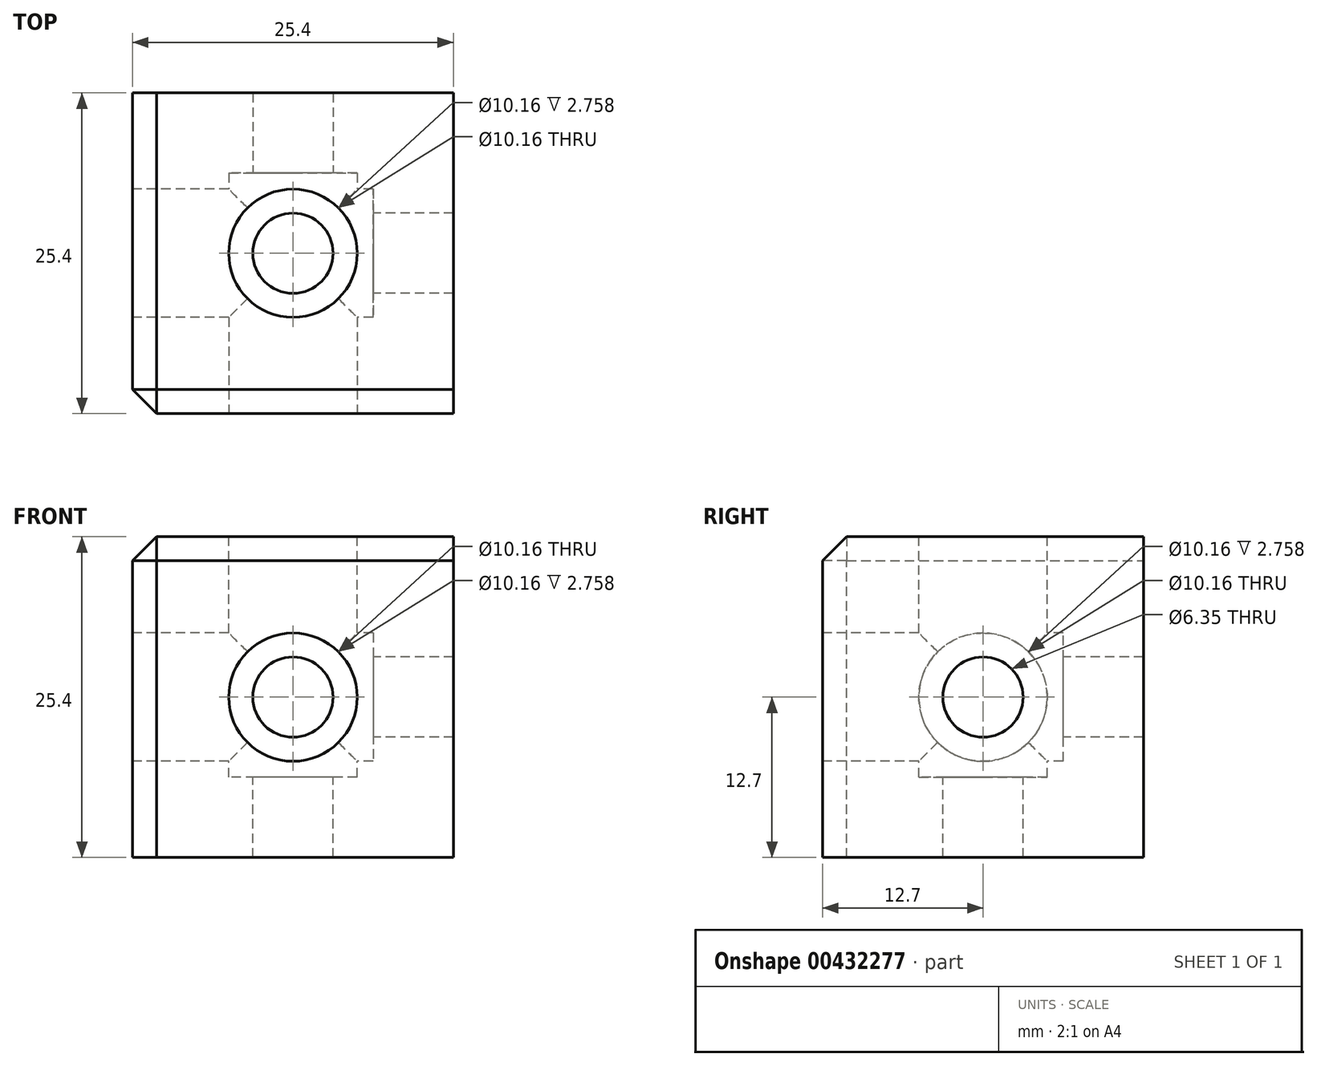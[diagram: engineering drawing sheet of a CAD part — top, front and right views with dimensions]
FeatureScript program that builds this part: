
annotation { "Feature Type Name" : "Feature", "Feature Type Description" : "" }
export const myFeature = defineFeature(function(context is Context, id is Id, definition is map)
    precondition{}
    {
        {
            var Q0;
            Q0=qCreatedBy(makeId("Top.planeOp"),FACE);
            var sketch = newSketch(context, id + "F0", { "sketchPlane" : qUnion([Q0])});
            skLineSegment(sketch, "E0.bottom", {"start": v(12.7, 12.7) * mm, "end": v(-12.7, 12.7) * mm});
            skLineSegment(sketch, "E0.top", {"start": v(12.7, -12.7) * mm, "end": v(-12.7, -12.7) * mm});
            skLineSegment(sketch, "E0.left", {"start": v(12.7, 12.7) * mm, "end": v(12.7, -12.7) * mm});
            skLineSegment(sketch, "E0.right", {"start": v(-12.7, 12.7) * mm, "end": v(-12.7, -12.7) * mm});
            skPoint(sketch, "E0.middle", {"position": v(0, 0) * mm});
            skSolve(sketch);
        }
        {
            var Q0;
            Q0 = qSketchRegion(id + "F0", true);
            extrude(context, id + "F1", {"entities" : qUnion([Q0]), "depth" : 25.4 * mm});
        }
        {
            var Q0;
            Q0=makeQuery(id+"F1.opExtrude","CAP_FACE",FACE,{"disambiguationData":[OSD([sQuery(id+"F0.wireOp",EDGE,"E0.bottom"),sQuery(id+"F0.wireOp",EDGE,"E0.top"),sQuery(id+"F0.wireOp",EDGE,"E0.left"),sQuery(id+"F0.wireOp",EDGE,"E0.right")])],"isStart":false});
            var sketch = newSketch(context, id + "F2", { "sketchPlane" : qUnion([Q0])});
            skPoint(sketch, "E1", {"position": v(0, 0) * mm});
            skSolve(sketch);
        }
        {
            var Q0;
            Q0=makeQuery(id+"F1.opExtrude","SWEPT_FACE",FACE,{"disambiguationData":[OSD([sQuery(id+"F0.wireOp",EDGE,"E0.top")])]});
            var sketch = newSketch(context, id + "F3", { "sketchPlane" : qUnion([Q0])});
            skPoint(sketch, "E2", {"position": v(0, 12.7) * mm});
            skPoint(sketch, "E2.positionSnap0", {"position": v(-12.7, 12.7) * mm});
            skSolve(sketch);
        }
        {
            var Q0;
            Q0=makeQuery(id+"F1.opExtrude","SWEPT_FACE",FACE,{"disambiguationData":[OSD([sQuery(id+"F0.wireOp",EDGE,"E0.right")])]});
            var sketch = newSketch(context, id + "F4", { "sketchPlane" : qUnion([Q0])});
            skPoint(sketch, "E3", {"position": v(0, 12.7) * mm});
            skPoint(sketch, "E3.positionSnap0", {"position": v(-12.7, 12.7) * mm});
            skSolve(sketch);
        }
        {
            var Q0;
            Q0=sQuery(id+"F2.wireOp",VERTEX,"E1");
            var Q1;
            Q1=sQuery(id+"F4.wireOp",VERTEX,"E3");
            var Q2;
            Q2=sQuery(id+"F3.wireOp",VERTEX,"E2");
            var Q3;
            Q3=makeQuery(id+"F1.opExtrude","SWEPT_BODY",BODY,{"disambiguationData":[OSD([sQuery(id+"F0.wireOp",EDGE,"E0.bottom"),sQuery(id+"F0.wireOp",EDGE,"E0.top"),sQuery(id+"F0.wireOp",EDGE,"E0.left"),sQuery(id+"F0.wireOp",EDGE,"E0.right")])]});
            hole(context, id + "F5", {"style" : HoleStyle.C_BORE, "endStyle" : HoleEndStyle.THROUGH, "holeDiameter" : 6.35 * mm, "cBoreDiameter" : 10.16 * mm, "cBoreDepth" : 19.05 * mm, "isTappedThrough" : true, "tappedDepth" : 38.6 * mm, "tapClearance" : 3, "startFromSketch" : true, "locations" : qUnion([Q0, Q1, Q2]), "scope" : qUnion([Q3])});
        }
        {
            var Q0;
            Q0=makeQuery(id+"F1.opExtrude","CAP_EDGE",EDGE,{"disambiguationData":[OSD([sQuery(id+"F0.wireOp",EDGE,"E0.right")])],"isStart":false});
            var Q1;
            Q1=makeQuery(id+"F1.opExtrude","CAP_EDGE",EDGE,{"disambiguationData":[OSD([sQuery(id+"F0.wireOp",EDGE,"E0.top")])],"isStart":false});
            var Q2;
            Q2=makeQuery(id+"F1.opExtrude","SWEPT_EDGE",EDGE,{"disambiguationData":[OSD([sQuery(id+"F0.wireOp",EDGE,"E0.top"),sQuery(id+"F0.wireOp",EDGE,"E0.right")])]});
            chamfer(context, id + "F6", {"entities" : qUnion([Q0, Q1, Q2]), "width" : 1.9 * mm, "tangentPropagation" : true});
        }
    });
